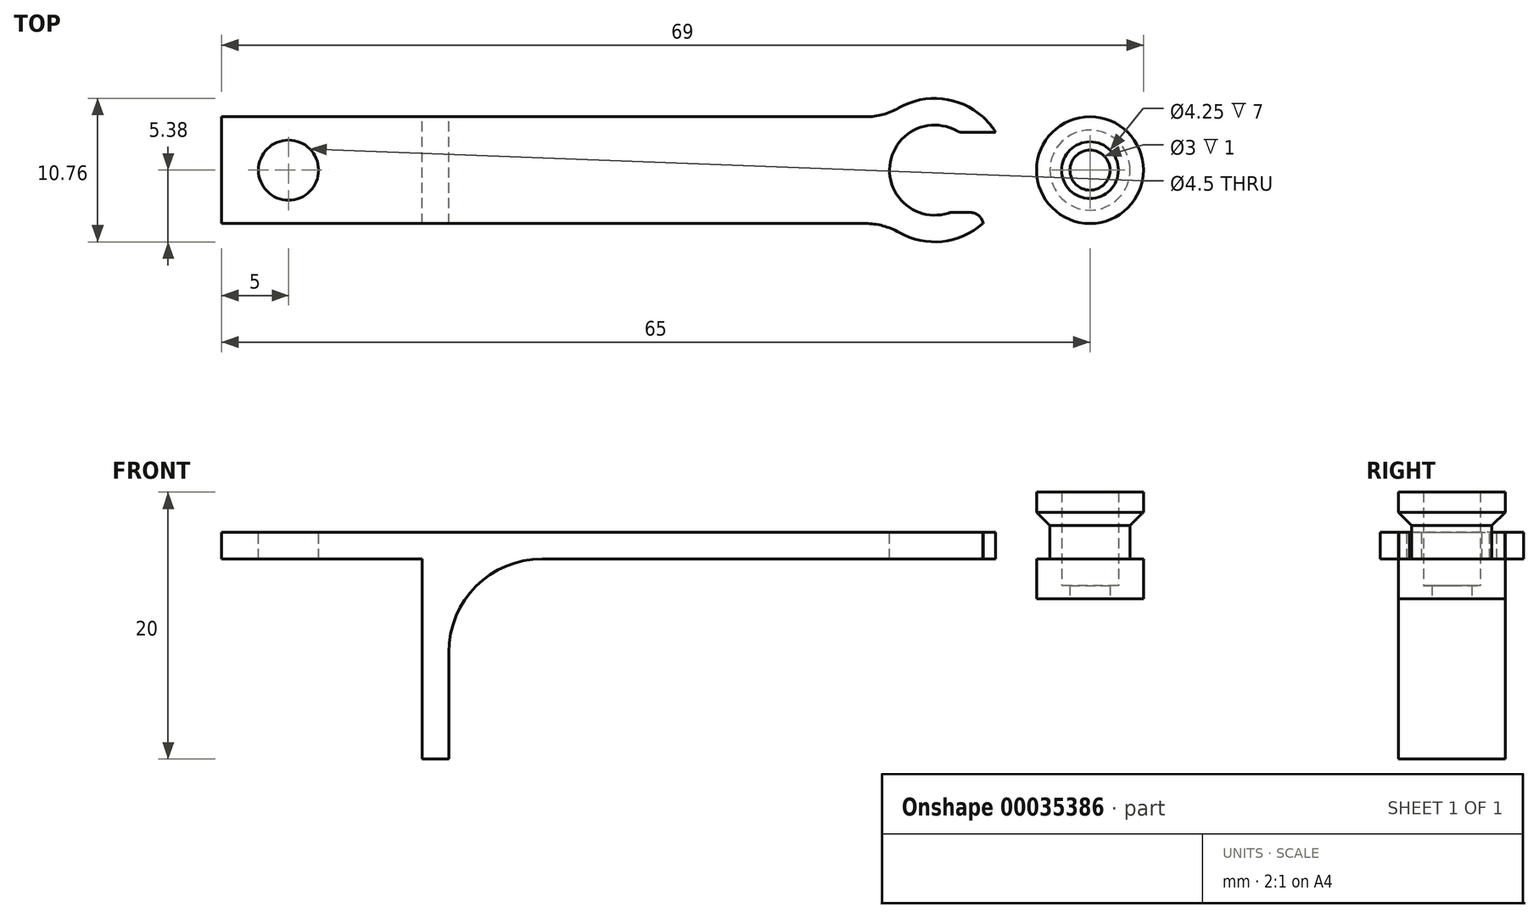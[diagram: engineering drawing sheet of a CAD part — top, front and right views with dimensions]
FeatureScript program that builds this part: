
annotation { "Feature Type Name" : "Feature", "Feature Type Description" : "" }
export const myFeature = defineFeature(function(context is Context, id is Id, definition is map)
    precondition{}
    {
        {
            var Q0;
            Q0=qCreatedBy(makeId("Front.planeOp"),FACE);
            var sketch = newSketch(context, id + "F0", { "sketchPlane" : qUnion([Q0])});
            skLineSegment(sketch, "E0", {"start": v(0, 0) * mm, "end": v(40, 0) * mm});
            skLineSegment(sketch, "E1", {"start": v(40, 0) * mm, "end": v(40, 2) * mm});
            skLineSegment(sketch, "E2", {"start": v(40, 2) * mm, "end": v(0, 2) * mm});
            skLineSegment(sketch, "E3", {"start": v(0, 2) * mm, "end": v(-17, 2) * mm});
            skLineSegment(sketch, "E4", {"start": v(-17, 2) * mm, "end": v(-17, 0) * mm});
            skLineSegment(sketch, "E5", {"start": v(-17, 0) * mm, "end": v(-2, 0) * mm});
            skLineSegment(sketch, "E6", {"start": v(-2, 0) * mm, "end": v(-2, -15) * mm});
            skLineSegment(sketch, "E7", {"start": v(-2, -15) * mm, "end": v(0, -15) * mm});
            skLineSegment(sketch, "E8", {"start": v(0, -15) * mm, "end": v(0, 0) * mm});
            skSolve(sketch);
        }
        {
            var Q0;
            Q0=makeQuery(id+"F0.imprint","IMPRINT",FACE,{"disambiguationData":[TD([[makeQuery(id+"F0.imprint","IMPRINT",EDGE,{"derivedFrom":sQuery(id+"F0.wireOp",EDGE,"E0")}),1.0]])]});
            extrude(context, id + "F1", {"entities" : qUnion([Q0]), "endBound" : BoundingType.SYMMETRIC, "depth" : 8 * mm});
        }
        {
            var Q0;
            Q0=makeQuery(id+"F1.opExtrude","SWEPT_FACE",FACE,{"disambiguationData":[OSD([sQuery(id+"F0.wireOp",EDGE,"E2"),sQuery(id+"F0.wireOp",EDGE,"E3")])]});
            var sketch = newSketch(context, id + "F2", { "sketchPlane" : qUnion([Q0])});
            skCircle(sketch, "E9.converted", {"center": v(36.38, 0) * mm, "radius": 5.38 * mm});
            skSolve(sketch);
        }
        {
            var Q0;
            Q0 = qSketchRegion(id + "F2", true);
            var Q1;
            Q1=makeQuery(id+"F1.opExtrude","SWEPT_FACE",FACE,{"disambiguationData":[OSD([sQuery(id+"F0.wireOp",EDGE,"E0")])]});
            extrude(context, id + "F3", {"entities" : qUnion([Q0]), "operationType" : NewBodyOperationType.ADD, "endBound" : BoundingType.UP_TO_SURFACE, "oppositeDirection" : true, "endBoundEntityFace" : qUnion([Q1]), "depth" : 25 * mm});
        }
        {
            var Q0;
            Q0=makeQuery(id+"F1.opExtrude","SWEPT_FACE",FACE,{"disambiguationData":[OSD([sQuery(id+"F0.wireOp",EDGE,"E2"),sQuery(id+"F0.wireOp",EDGE,"E3")])]});
            var sketch = newSketch(context, id + "F4", { "sketchPlane" : qUnion([Q0])});
            skArc(sketch, "E10", {"start": v(38.21, 2.83) * mm, "mid": v(33.02, 0.38) * mm, "end": v(37.53, -3.17) * mm});
            skLineSegment(sketch, "E11", {"start": v(43, 2.83) * mm, "end": v(43, 0) * mm});
            skPoint(sketch, "E11.endSnap0", {"position": v(40, 0) * mm});
            skLineSegment(sketch, "E12.MirrorCS", {"start": v(43, -3.17) * mm, "end": v(43, 0) * mm});
            skArc(sketch, "E13.MirrorC", {"start": v(37.53, -3.17) * mm, "mid": v(33.02, 0.38) * mm, "end": v(38.21, 2.83) * mm});
            skLineSegment(sketch, "E14", {"start": v(38.21, 2.83) * mm, "end": v(43, 2.83) * mm});
            skLineSegment(sketch, "E15", {"start": v(37.53, -3.17) * mm, "end": v(43, -3.17) * mm});
            skPoint(sketch, "E16.orphan", {"position": v(43, 5.09) * mm});
            skPoint(sketch, "E17.end.orphan", {"position": v(43, -5.09) * mm});
            skSolve(sketch);
        }
        {
            var Q0;
            Q0=makeQuery(id+"F4.imprint","IMPRINT",FACE,{"disambiguationData":[TD([[makeQuery(id+"F4.imprint","IMPRINT",EDGE,{"derivedFrom":sQuery(id+"F4.wireOp",EDGE,"E10")}),1.0]])]});
            var Q1;
            {var subQ5=sQuery(id+"F4.wireOp",EDGE,"E13.MirrorC");Q1=makeQuery(id+"F4.imprint","IMPRINT",FACE,{"disambiguationData":[TD([[makeQuery(id+"F4.imprint","IMPRINT",EDGE,{"derivedFrom":subQ5}),-1.0]])]});}
            extrude(context, id + "F5", {"entities" : qUnion([Q0, Q1]), "operationType" : NewBodyOperationType.REMOVE, "endBound" : BoundingType.THROUGH_ALL, "oppositeDirection" : true, "depth" : 25 * mm});
        }
        {
            var Q0;
            Q0=makeQuery(id+"F1.opExtrude","SWEPT_EDGE",EDGE,{"disambiguationData":[OSD([sQuery(id+"F0.wireOp",EDGE,"E0"),sQuery(id+"F0.wireOp",EDGE,"E8")])]});
            fillet(context, id + "F6", {"entities" : qUnion([Q0]), "radius" : 7 * mm, "tangentPropagation" : true, "allowEdgeOverflow" : false});
        }
        {
            var Q0;
            Q0=makeQuery(id+"F5.boolean.opBoolean","COPY",EDGE,{"derivedFrom":makeQuery(id+"F5.opExtrude","SWEPT_EDGE",EDGE,{"disambiguationData":[OSD([sQuery(id+"F4.wireOp",EDGE,"E13.MirrorC"),sQuery(id+"F4.wireOp",EDGE,"E14")])]})});
            var Q1;
            Q1=makeQuery(id+"F5.boolean.opBoolean","COPY",EDGE,{"derivedFrom":makeQuery(id+"F5.opExtrude","SWEPT_EDGE",EDGE,{"disambiguationData":[OSD([sQuery(id+"F4.wireOp",EDGE,"E13.MirrorC"),sQuery(id+"F4.wireOp",EDGE,"E15")])]})});
            var Q2;
            Q2=makeQuery(id+"F5.boolean.opBoolean","COPY",EDGE,{"derivedFrom":makeQuery(id+"F5.opExtrude","SWEPT_EDGE",EDGE,{"disambiguationData":[OSD([sQuery(id+"F2.wireOp",EDGE,"E9.converted"),sQuery(id+"F4.wireOp",EDGE,"E15")])]})});
            var Q3;
            Q3=makeQuery(id+"F5.boolean.opBoolean","COPY",EDGE,{"derivedFrom":makeQuery(id+"F5.opExtrude","SWEPT_EDGE",EDGE,{"disambiguationData":[OSD([sQuery(id+"F2.wireOp",EDGE,"E9.converted"),sQuery(id+"F4.wireOp",EDGE,"E14")])]})});
            fillet(context, id + "F7", {"entities" : qUnion([Q0, Q1, Q2, Q3]), "radius" : 1 * mm, "tangentPropagation" : true, "allowEdgeOverflow" : false});
        }
        {
            var Q0;
            Q0=makeQuery(id+"F1.opExtrude","SWEPT_FACE",FACE,{"disambiguationData":[OSD([sQuery(id+"F0.wireOp",EDGE,"E2"),sQuery(id+"F0.wireOp",EDGE,"E3")])]});
            var sketch = newSketch(context, id + "F8", { "sketchPlane" : qUnion([Q0])});
            skCircle(sketch, "E18", {"center": v(-12, 0) * mm, "radius": 2.25 * mm});
            skSolve(sketch);
        }
        {
            var Q0;
            Q0=makeQuery(id+"F8.imprint","IMPRINT",FACE,{"disambiguationData":[TD([[makeQuery(id+"F8.imprint","IMPRINT",EDGE,{"derivedFrom":sQuery(id+"F8.wireOp",EDGE,"E18")}),1.0]])]});
            extrude(context, id + "F9", {"entities" : qUnion([Q0]), "operationType" : NewBodyOperationType.REMOVE, "endBound" : BoundingType.THROUGH_ALL, "oppositeDirection" : true, "depth" : 25 * mm});
        }
        {
            var Q0;
            Q0=qCreatedBy(makeId("Top.planeOp"),FACE);
            var sketch = newSketch(context, id + "F10", { "sketchPlane" : qUnion([Q0])});
            skCircle(sketch, "E19", {"center": v(48, 0) * mm, "radius": 2.12 * mm});
            skCircle(sketch, "E20", {"center": v(48, 0) * mm, "radius": 3 * mm});
            skCircle(sketch, "E21", {"center": v(48, 0) * mm, "radius": 4 * mm});
            skSolve(sketch);
        }
        {
            var Q0;
            Q0=makeQuery(id+"F10.imprint","IMPRINT",FACE,{"disambiguationData":[TD([[makeQuery(id+"F10.imprint","IMPRINT",EDGE,{"derivedFrom":sQuery(id+"F10.wireOp",EDGE,"E19")}),-1.0]])]});
            extrude(context, id + "F11", {"entities" : qUnion([Q0]), "depth" : 5 * mm, "hasSecondDirection" : true, "secondDirectionOppositeDirection" : true, "secondDirectionDepth" : 3 * mm});
        }
        {
            var Q0;
            Q0=makeQuery(id+"F10.imprint","IMPRINT",FACE,{"disambiguationData":[TD([[makeQuery(id+"F10.imprint","IMPRINT",EDGE,{"derivedFrom":sQuery(id+"F10.wireOp",EDGE,"E20")}),-1.0]])]});
            var Q1;
            Q1=makeQuery(id+"F11.opExtrude","CAP_FACE",FACE,{"disambiguationData":[OSD([sQuery(id+"F10.wireOp",EDGE,"E19"),sQuery(id+"F10.wireOp",EDGE,"E20")])],"isStart":true});
            extrude(context, id + "F12", {"entities" : qUnion([Q0]), "operationType" : NewBodyOperationType.ADD, "endBound" : BoundingType.UP_TO_SURFACE, "oppositeDirection" : true, "endBoundEntityFace" : qUnion([Q1]), "depth" : 1 * mm});
        }
        {
            var Q0;
            Q0=makeQuery(id+"F11.opExtrude","CAP_FACE",FACE,{"disambiguationData":[OSD([sQuery(id+"F10.wireOp",EDGE,"E19"),sQuery(id+"F10.wireOp",EDGE,"E20")])],"isStart":false});
            var sketch = newSketch(context, id + "F13", { "sketchPlane" : qUnion([Q0])});
            skCircle(sketch, "E22.0", {"center": v(48, 0) * mm, "radius": 4 * mm});
            skCircle(sketch, "E23.0.0", {"center": v(48, 0) * mm, "radius": 3 * mm});
            skSolve(sketch);
        }
        {
            var Q0;
            Q0=makeQuery(id+"F13.imprint","IMPRINT",FACE,{"disambiguationData":[TD([[makeQuery(id+"F13.imprint","IMPRINT",EDGE,{"derivedFrom":sQuery(id+"F13.wireOp",EDGE,"E22.0")}),1.0]])]});
            extrude(context, id + "F14", {"entities" : qUnion([Q0]), "operationType" : NewBodyOperationType.ADD, "oppositeDirection" : true, "depth" : 2.5 * mm});
        }
        {
            var Q0;
            {var subQ0=sQuery(id+"F10.wireOp",EDGE,"E20");Q0=makeQuery(id+"F12.boolean.opBoolean","MERGE",FACE,{"derivedFrom":[makeQuery(id+"F11.opExtrude","CAP_FACE",FACE,{"disambiguationData":[OSD([sQuery(id+"F10.wireOp",EDGE,"E19"),subQ0])],"isStart":true}),makeQuery(id+"F12.opExtrude","CAP_FACE",FACE,{"disambiguationData":[OSD([subQ0,sQuery(id+"F10.wireOp",EDGE,"E21")])],"isStart":false})]});}
            var sketch = newSketch(context, id + "F15", { "sketchPlane" : qUnion([Q0])});
            skCircle(sketch, "E24", {"center": v(48, 0) * mm, "radius": 1.5 * mm});
            skCircle(sketch, "E25.0", {"center": v(48, 0) * mm, "radius": 4 * mm});
            skSolve(sketch);
        }
        {
            var Q0;
            Q0=makeQuery(id+"F15.imprint","IMPRINT",FACE,{"disambiguationData":[TD([[makeQuery(id+"F15.imprint","IMPRINT",EDGE,{"derivedFrom":sQuery(id+"F15.wireOp",EDGE,"E24")}),-1.0]])]});
            extrude(context, id + "F16", {"entities" : qUnion([Q0]), "operationType" : NewBodyOperationType.ADD, "oppositeDirection" : true, "depth" : 1 * mm});
        }
        {
            var Q0;
            Q0=makeQuery(id+"F14.opExtrude","CAP_EDGE",EDGE,{"disambiguationData":[OSD([sQuery(id+"F13.wireOp",EDGE,"E22.0")])],"isStart":false});
            chamfer(context, id + "F17", {"entities" : qUnion([Q0]), "width" : 1 * mm, "tangentPropagation" : true});
        }
        {
            var Q0;
            Q0=makeQuery(id+"F3.boolean.opBoolean","INTERSECT",EDGE,{"disambiguationData":[OD(0.0)],"derivedFrom":[makeQuery(id+"F1.opExtrude","CAP_FACE",FACE,{"disambiguationData":[OSD([sQuery(id+"F0.wireOp",EDGE,"E0"),sQuery(id+"F0.wireOp",EDGE,"E1"),sQuery(id+"F0.wireOp",EDGE,"E2"),sQuery(id+"F0.wireOp",EDGE,"E3"),sQuery(id+"F0.wireOp",EDGE,"E4"),sQuery(id+"F0.wireOp",EDGE,"E5"),sQuery(id+"F0.wireOp",EDGE,"E6"),sQuery(id+"F0.wireOp",EDGE,"E7"),sQuery(id+"F0.wireOp",EDGE,"E8")])],"isStart":true}),makeQuery(id+"F3.opExtrude","SWEPT_FACE",FACE,{"disambiguationData":[OSD([sQuery(id+"F2.wireOp",EDGE,"E9.converted")])]})]});
            var Q1;
            Q1=makeQuery(id+"F3.boolean.opBoolean","INTERSECT",EDGE,{"disambiguationData":[OD(0.0)],"derivedFrom":[makeQuery(id+"F1.opExtrude","CAP_FACE",FACE,{"disambiguationData":[OSD([sQuery(id+"F0.wireOp",EDGE,"E0"),sQuery(id+"F0.wireOp",EDGE,"E1"),sQuery(id+"F0.wireOp",EDGE,"E2"),sQuery(id+"F0.wireOp",EDGE,"E3"),sQuery(id+"F0.wireOp",EDGE,"E4"),sQuery(id+"F0.wireOp",EDGE,"E5"),sQuery(id+"F0.wireOp",EDGE,"E6"),sQuery(id+"F0.wireOp",EDGE,"E7"),sQuery(id+"F0.wireOp",EDGE,"E8")])],"isStart":false}),makeQuery(id+"F3.opExtrude","SWEPT_FACE",FACE,{"disambiguationData":[OSD([sQuery(id+"F2.wireOp",EDGE,"E9.converted")])]})]});
            fillet(context, id + "F18", {"entities" : qUnion([Q0, Q1]), "radius" : 5 * mm, "tangentPropagation" : true, "allowEdgeOverflow" : false});
        }
    });
